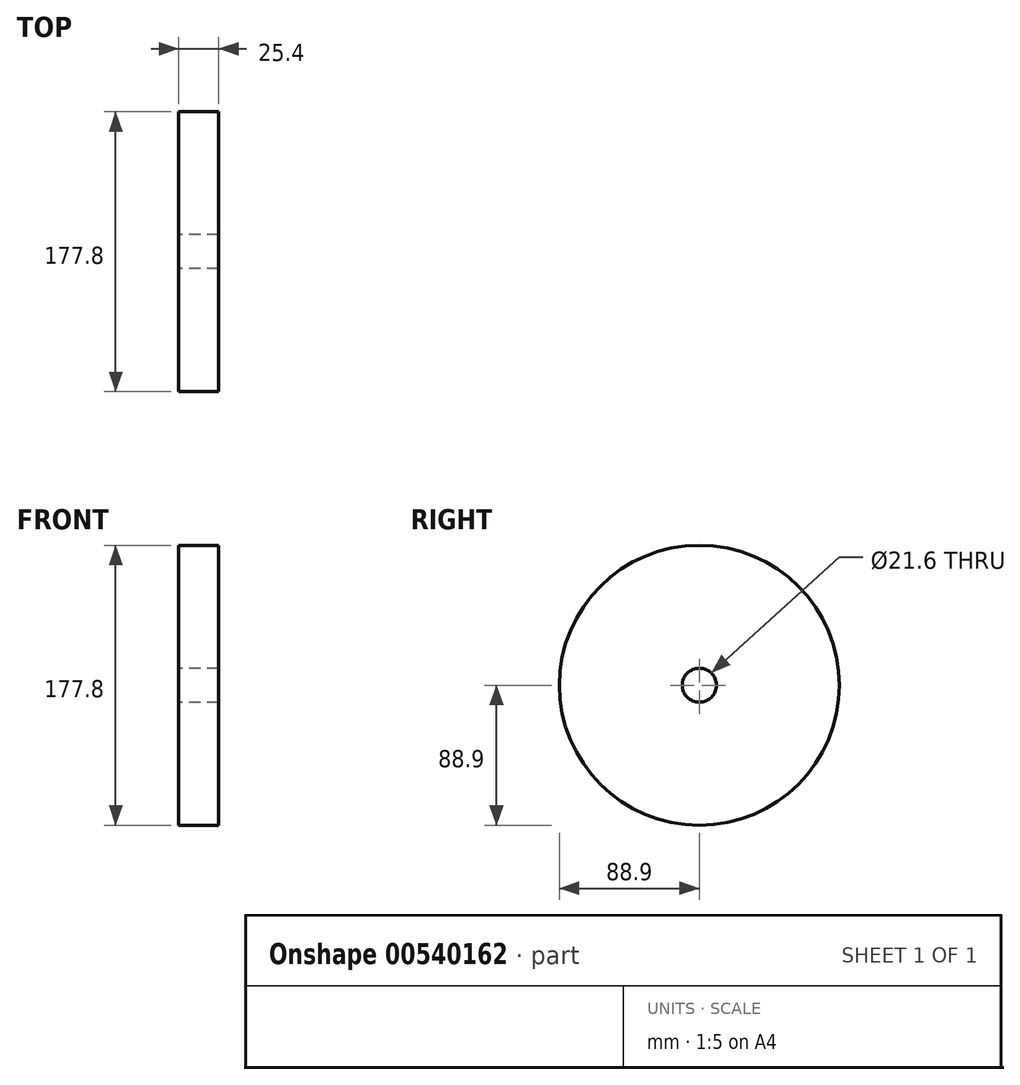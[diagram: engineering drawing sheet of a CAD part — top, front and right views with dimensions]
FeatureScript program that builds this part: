
annotation { "Feature Type Name" : "Feature", "Feature Type Description" : "" }
export const myFeature = defineFeature(function(context is Context, id is Id, definition is map)
    precondition{}
    {
        {
            var Q0;
            Q0=qCreatedBy(makeId("Right.planeOp"),FACE);
            var sketch = newSketch(context, id + "F0", { "sketchPlane" : qUnion([Q0])});
            skCircle(sketch, "E0", {"center": v(0, 0) * mm, "radius": 88.9 * mm});
            skCircle(sketch, "E1", {"center": v(0, 0) * mm, "radius": 10.8 * mm});
            skSolve(sketch);
        }
        {
            var Q0;
            Q0 = qSketchRegion(id + "F0", true);
            extrude(context, id + "F1", {"entities" : qUnion([Q0]), "depth" : 25.4 * mm, "offsetDistance" : 25.4 * mm});
        }
    });
